# Revit family: R62 - Wall Based
name_source: partatom
category: Puertas
revit_build: Autodesk Revit 2014 (Build: 20130308_1515(x64)
units: mm (PartAtom-declared; Revit-internal decimal feet)

## types (6) — shared parameters
AccessibilityPerformance = 4-6/min.
AccessoryOptions = contact manufacturer
AntiFingerTrapRequirement = No
BIMObjectName = agtatec_Record_SldngDrset_R62 SecurityDoor_WallBased
Capacity = 4-6/min.
Category = Security gate/portal
Colour = Aluminium
Código de montaje = B2030300
Descripción = Circular sliding door
DoorNumber = 2
DoorsetOperation = automatic
DrumWallPanelFill = agtatec_Record_Revolving Door, Laminated Safety Glass (Clear)
DurationUnit = Year
ElectronicLock = Sí
Features = Separation, anti-tailgating, anti-piggybacking
Finish = Powder coated, Anodized, customer specific
FireExit = No
Flooring = agtatec_Record_Revolving Door, Felt Carpet
FrameFinishOptions = Stainless steel and more
FrameMaterial = Aluminium
FrameProfile = Aluminium
FrameSeal = Sí
Función = Exterior
GlassLayers = 2
GlassThickness1 = 8
GlassThickness2 = 10
GlassType = part of glazing spec
HasDrive = Sí
IfcExportAs = IFCDoorStyle
IfcExportType = Door
IsExternal = Sí
IssueDate = <>
LeafColourOptions = all RAL, customer specific
LeafPanelFill = agtatec_Record_Revolving Door, Laminated Safety Glass (Clear)
ManufacturerName = record
ManufacturerURL = www.agta-record.com
Material = Aluminium
ModelReference = depends on the configuration
Modelo = R62
NBSDescription = Sliding Doorset
NBSReference = 25-50-20/175
Name = SldngDrset_R62-SecurityDoor_Generic_Record
NominalHeight = 640080 mm
OpenEntry = No
OpenExit = No
Operación = automatic
PanelFrames = agtatec_Record_Revolving Door, Aluminium
ProductInformation = www.agta-record.com
ReferenceStandard = EN16005, EN16361, DIN 18650, etc.
ReplacementCost = Depends on the configuration and door type
SafetyDevices = Optical sensors
SelfClosing = Sí
ServiceLifeDuration = 10-15 years
Shape = Cylinder Shaped
Size = XxxXXxXX
SmokeStop = No
ThresholdRequired = No
Tipo de construcción = Automatic Revolving Door
URL = www.agta-record.com
Uniclass2 = Ss_25_30_20_77
Version = 1
WarrantyDescription = Depends on country
WarrantyDurationLabour = Depends on country
WarrantyDurationParts = Depends on country
WarrantyDurationUnit = Depends on country
WarrantyGuarantorLabour = Local door manufacturer
WarrantyGuarantorParts = Local door manufacturer
WithinStandardSizes = Sí
zero-valued in all types: Costo, GlazingAreaFraction, Grosor, OffsetFromWallSide, OffsetFromWallTop, ThermalTransmittance

## per-type parameters (varying)
| type | Altura | Altura aproximada | Anchura | Anchura aproximada | CanopyHeight | CanopyRadius | DiameterOptions | HandicapAccessible | InsideDiameter | NominalLength | NominalWidth | OuterRadius | OutsideDiameter | PassageHeight | PassageWidth | PassageWidthOptions | RecessHeight | RecessWidth | TotalDiameter | TotalHeight | WallCutHeight | Weight |
| Record R62 600 - Double | 2420 mm | 2426 mm | 1115 mm  [stored 3.65814 ft] | 1252.3 mm | 220 mm  [stored 0.721785 ft] | 548 mm  [stored 1.7979 ft] | 1035mm, 1090mm depends on glas type | No | 967 mm | 315468 mm | 315468 mm | 545 mm  [stored 1.78806 ft] | 1090 mm  [stored 3.57612 ft] | 2200 mm | 469.1 mm  [stored 1.53904 ft] | 600 | 2470 mm | 1298.2 mm  [stored 4.25919 ft] | 1198.2 mm  [stored 3.9311 ft] | 2420 mm | 2475 mm | ca. 355-475kg |
| Record R62 900 - Double | 3210 mm | 3216 mm | 1535 mm  [stored 5.03609 ft] | 1672.3 mm | 610 mm  [stored 2.00131 ft] | 758 mm  [stored 2.48688 ft] | 1455mm, 1510mm depends on glas type | Sí | 1387 mm  [stored 4.55052 ft] | 443484 mm | 443484 mm | 755 mm  [stored 2.47703 ft] | 1510 mm  [stored 4.95407 ft] | 2600 mm | 679.1 mm  [stored 2.22802 ft] | 900 | 3260 mm | 1718.2 mm | 1618.2 mm | 3210 mm | 3265 mm | ca. 460-640kg |
| Record R62 1100 - Double | 4000 mm | 4006 mm | 1815 mm | 1952.3 mm | 1000 mm  [stored 3.28084 ft] | 898 mm  [stored 2.94619 ft] | 1735mm, 1790mm depends on glas type | Sí | 1667 mm | 528828 mm | 528828 mm | 895 mm  [stored 2.93635 ft] | 1790 mm | 3000 mm | 819.1 mm  [stored 2.68734 ft] | 1100 | 4050 mm | 1998.2 mm | 1898.2 mm | 4000 mm | 4055 mm | ca. 538-760kg |
| Record R62 1100 - Single | 4000 mm | 4006 mm | 1760 mm | 1897.3 mm | 1000 mm  [stored 3.28084 ft] | 870.5 mm  [stored 2.85597 ft] | 1735mm, 1790mm depends on glas type | Sí | 1612 mm | 528828 mm | 528828 mm | 867.5 mm  [stored 2.84613 ft] | 1735 mm | 3000 mm | 791.6 mm  [stored 2.59711 ft] | 1100 | 4050 mm | 1943.2 mm | 1843.2 mm | 4000 mm | 4055 mm | ca. 538-760kg |
| Record R62 900 - Single | 3210 mm | 3216 mm | 1480 mm  [stored 4.85564 ft] | 1617.3 mm | 610 mm  [stored 2.00131 ft] | 730.5 mm  [stored 2.39665 ft] | 1455mm, 1510mm depends on glas type | Sí | 1332 mm  [stored 4.37008 ft] | 443484 mm | 443484 mm | 727.5 mm  [stored 2.38681 ft] | 1455 mm  [stored 4.77362 ft] | 2600 mm | 651.6 mm  [stored 2.1378 ft] | 900 | 3260 mm | 1663.2 mm | 1563.2 mm | 3210 mm | 3265 mm | ca. 460-640kg |
| Record R62 600 - Single | 2420 mm | 2426 mm | 1060 mm | 1197.3 mm | 220 mm  [stored 0.721785 ft] | 520.5 mm | 1035mm, 1090mm depends on glas type | No | 912 mm | 315468 mm | 315468 mm | 517.5 mm | 1035 mm  [stored 3.39567 ft] | 2200 mm | 441.6 mm  [stored 1.44882 ft] | 600 | 2470 mm | 1243.2 mm  [stored 4.07874 ft] | 1143.2 mm | 2420 mm | 2475 mm | ca. 355-475kg |

note: [stored X ft] marks values corroborated as IEEE doubles in the binary element streams (Revit-internal decimal feet)

## geometry (parser evidence)
native form markers: Blend x4, Sweep x8
no freeform markers — native parametric forms only
